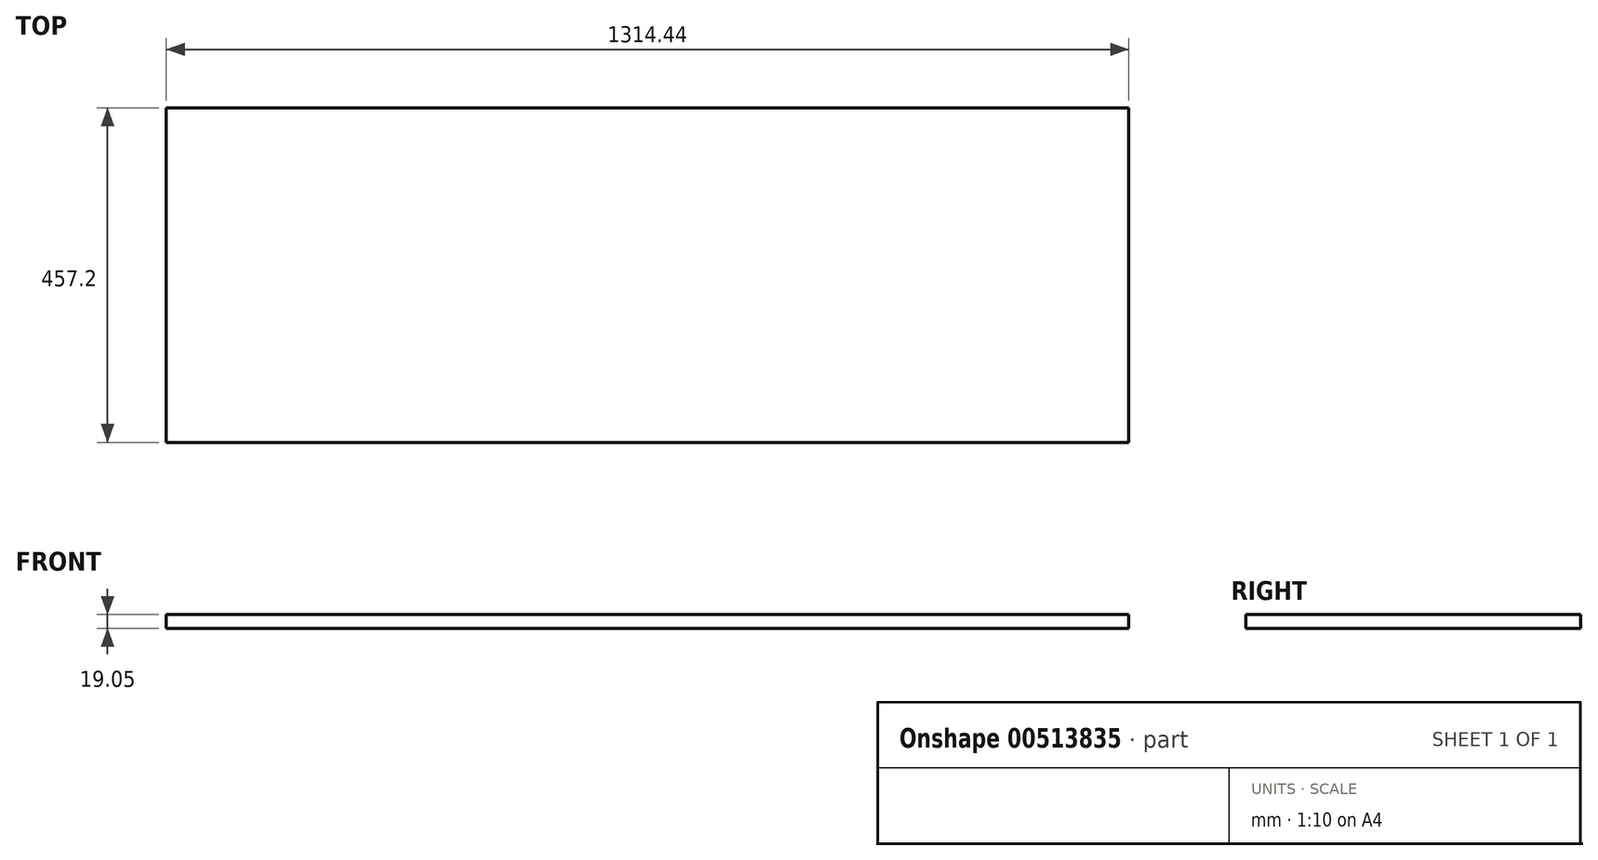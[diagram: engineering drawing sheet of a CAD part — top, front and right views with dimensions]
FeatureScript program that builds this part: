
annotation { "Feature Type Name" : "Feature", "Feature Type Description" : "" }
export const myFeature = defineFeature(function(context is Context, id is Id, definition is map)
    precondition{}
    {
        {
            var Q0;
            Q0=qCreatedBy(makeId("Top.planeOp"),FACE);
            var sketch = newSketch(context, id + "F0", { "sketchPlane" : qUnion([Q0])});
            skLineSegment(sketch, "E0.bottom", {"start": v(657.23, 228.6) * mm, "end": v(-657.23, 228.6) * mm});
            skLineSegment(sketch, "E0.top", {"start": v(657.23, -228.6) * mm, "end": v(-657.23, -228.6) * mm});
            skLineSegment(sketch, "E0.left", {"start": v(657.23, 228.6) * mm, "end": v(657.23, -228.6) * mm});
            skLineSegment(sketch, "E0.right", {"start": v(-657.23, 228.6) * mm, "end": v(-657.23, -228.6) * mm});
            skPoint(sketch, "E0.middle", {"position": v(0, 0) * mm});
            skSolve(sketch);
        }
        {
            var Q0;
            Q0 = qSketchRegion(id + "F0", true);
            extrude(context, id + "F1", {"entities" : qUnion([Q0]), "depth" : 19.05 * mm});
        }
    });
